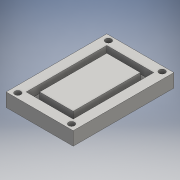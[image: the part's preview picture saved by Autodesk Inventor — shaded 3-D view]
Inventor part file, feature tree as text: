
AUTODESK INVENTOR PART (.ipt)
format: ipt  version: 2016 (Build 200138000, 138)  size: 128,000 bytes
history: native  units: mm
features: sketch x3, extrude x2, hole x1
ambient origin geometry x8: Origin, YZ Plane, XZ Plane, XY Plane, X Axis, Y Axis, Z Axis, Center Point
bodies: Solid1 (feature_tree)
feature tree (6):
  extrude  "Extrusion1"  Depth=75.0mm
  hole  "Hole1"  [1 undecoded]
  extrude  "Extrusion2"  Depth=6.0mm
  sketch  "Sketch1"  dims[d0=50.0mm d1=75.0mm]
  sketch  "Sketch2"  dims[d2=37.5mm d3=25.0mm]
  sketch  "Sketch3"  dims[d4=10.0mm d5=0.0mm d6=40.0mm d7=20.0mm d8=67.5mm d9=33.75mm d10=4.5mm d11=6.35mm d12=9.4mm d13=2.0mm d14=90.0deg d15=9.525mm d16=20.594885mm d19=35.0mm d22=60.0mm d23=30.0mm d24=5.0mm d26=17.5mm d27=5.0mm d29=5.0mm d30=5.0mm d31=6.0mm d32=0.0mm]
note: 1 required parameter value undecoded (feature->parameter linkage not recoverable at this tier; creation-order binding heuristic only, values carry confidence <= 0.55)
